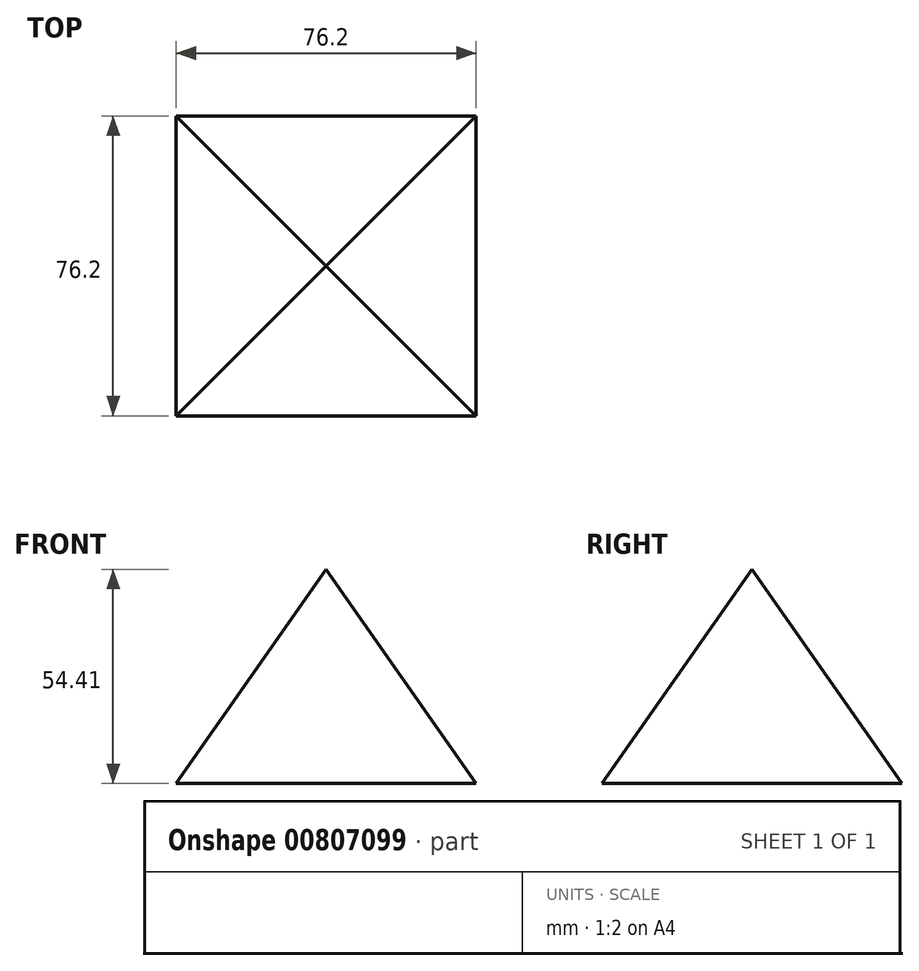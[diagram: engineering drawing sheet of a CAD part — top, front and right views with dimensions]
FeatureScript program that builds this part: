
annotation { "Feature Type Name" : "Feature", "Feature Type Description" : "" }
export const myFeature = defineFeature(function(context is Context, id is Id, definition is map)
    precondition{}
    {
        {
            var Q0;
            Q0=qCreatedBy(makeId("Top.planeOp"),FACE);
            var sketch = newSketch(context, id + "F0", { "sketchPlane" : qUnion([Q0])});
            skLineSegment(sketch, "E0.bottom", {"start": v(17.95, 0.58) * mm, "end": v(-58.25, 0.58) * mm});
            skLineSegment(sketch, "E0.top", {"start": v(17.95, 76.78) * mm, "end": v(-58.25, 76.78) * mm});
            skLineSegment(sketch, "E0.left", {"start": v(17.95, 0.58) * mm, "end": v(17.95, 76.78) * mm});
            skLineSegment(sketch, "E0.right", {"start": v(-58.25, 0.58) * mm, "end": v(-58.25, 76.78) * mm});
            skSolve(sketch);
        }
        {
            var Q0;
            Q0=makeQuery(id+"F0.imprint","IMPRINT",FACE,{"disambiguationData":[TD([[makeQuery(id+"F0.imprint","IMPRINT",EDGE,{"derivedFrom":sQuery(id+"F0.wireOp",EDGE,"E0.bottom")}),-1.0]])]});
            extrude(context, id + "F1", {"entities" : qUnion([Q0]), "depth" : 219.96 * mm, "offsetDistance" : 25.4 * mm, "hasDraft" : true, "draftAngle" : 35 * degree, "draftPullDirection" : true});
        }
    });
